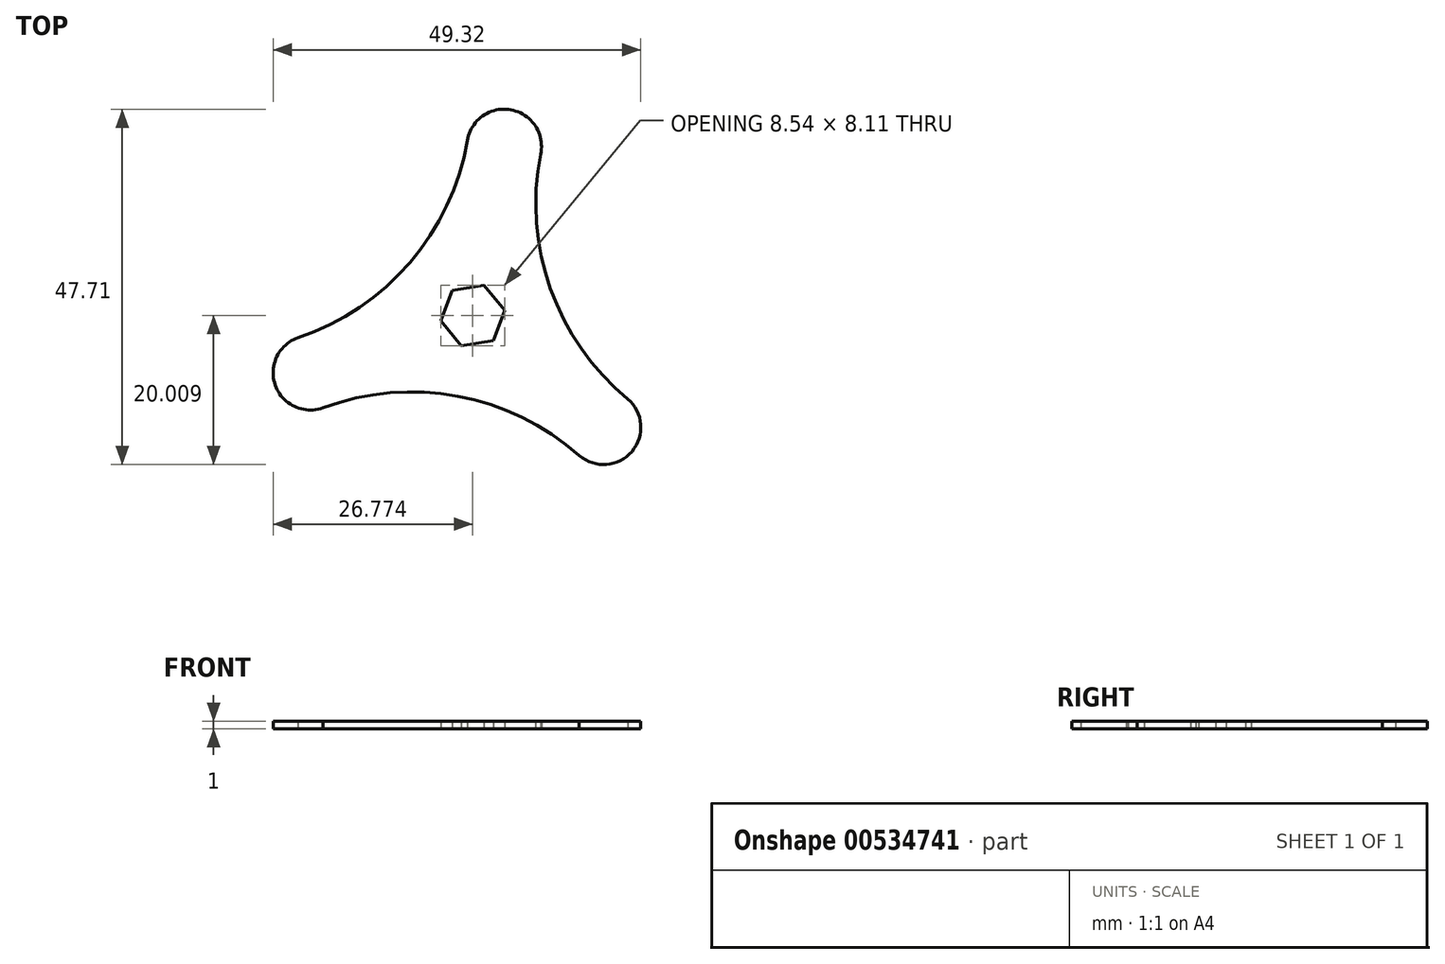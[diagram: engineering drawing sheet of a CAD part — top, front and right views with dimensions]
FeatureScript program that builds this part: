
annotation { "Feature Type Name" : "Feature", "Feature Type Description" : "" }
export const myFeature = defineFeature(function(context is Context, id is Id, definition is map)
    precondition{}
    {
        {
            var Q0;
            Q0=qCreatedBy(makeId("Top.planeOp"),FACE);
            var sketch = newSketch(context, id + "F0", { "sketchPlane" : qUnion([Q0])});
            skArc(sketch, "E0", {"start": v(41.65, 1.45) * mm, "mid": v(48.7, 2) * mm, "end": v(48.15, 9.05) * mm});
            skArc(sketch, "E1", {"start": v(41.65, 1.45) * mm, "mid": v(25.34, 9.42) * mm, "end": v(7.24, 7.85) * mm});
            skArc(sketch, "E2", {"start": v(3.91, 17.28) * mm, "mid": v(0.86, 10.9) * mm, "end": v(7.24, 7.85) * mm});
            skArc(sketch, "E3", {"start": v(3.91, 17.28) * mm, "mid": v(18.92, 27.37) * mm, "end": v(26.64, 43.73) * mm});
            skArc(sketch, "E4", {"start": v(36.47, 41.9) * mm, "mid": v(32.5, 47.88) * mm, "end": v(26.64, 43.73) * mm});
            skArc(sketch, "E5", {"start": v(36.47, 41.9) * mm, "mid": v(37.78, 23.86) * mm, "end": v(48.15, 9.05) * mm});
            skCircle(sketch, "E6", {"center": v(27.35, 20.26) * mm, "radius": 2.5 * mm});
            skCircle(sketch, "E7.cCircle", {"center": v(27.35, 20.26) * mm, "radius": 3.75 * mm, "construction": true});
            skLineSegment(sketch, "E7.0", {"start": v(31.62, 20.97) * mm, "end": v(30.1, 16.92) * mm});
            skLineSegment(sketch, "E7.1", {"start": v(30.1, 16.92) * mm, "end": v(25.84, 16.2) * mm});
            skLineSegment(sketch, "E7.2", {"start": v(25.84, 16.2) * mm, "end": v(23.08, 19.55) * mm});
            skLineSegment(sketch, "E7.3", {"start": v(23.08, 19.55) * mm, "end": v(24.6, 23.6) * mm});
            skLineSegment(sketch, "E7.4", {"start": v(24.6, 23.6) * mm, "end": v(28.87, 24.31) * mm});
            skLineSegment(sketch, "E7.5", {"start": v(28.87, 24.31) * mm, "end": v(31.62, 20.97) * mm});
            skPoint(sketch, "E7.0.midPoint", {"position": v(30.87, 18.94) * mm});
            skSolve(sketch);
        }
        {
            var Q0;
            Q0=makeQuery(id+"F0.imprint","IMPRINT",FACE,{"disambiguationData":[TD([[makeQuery(id+"F0.imprint","IMPRINT",EDGE,{"derivedFrom":sQuery(id+"F0.wireOp",EDGE,"E0")}),1.0]])]});
            extrude(context, id + "F1", {"entities" : qUnion([Q0]), "depth" : 1 * mm, "offsetDistance" : 25 * mm});
        }
    });
